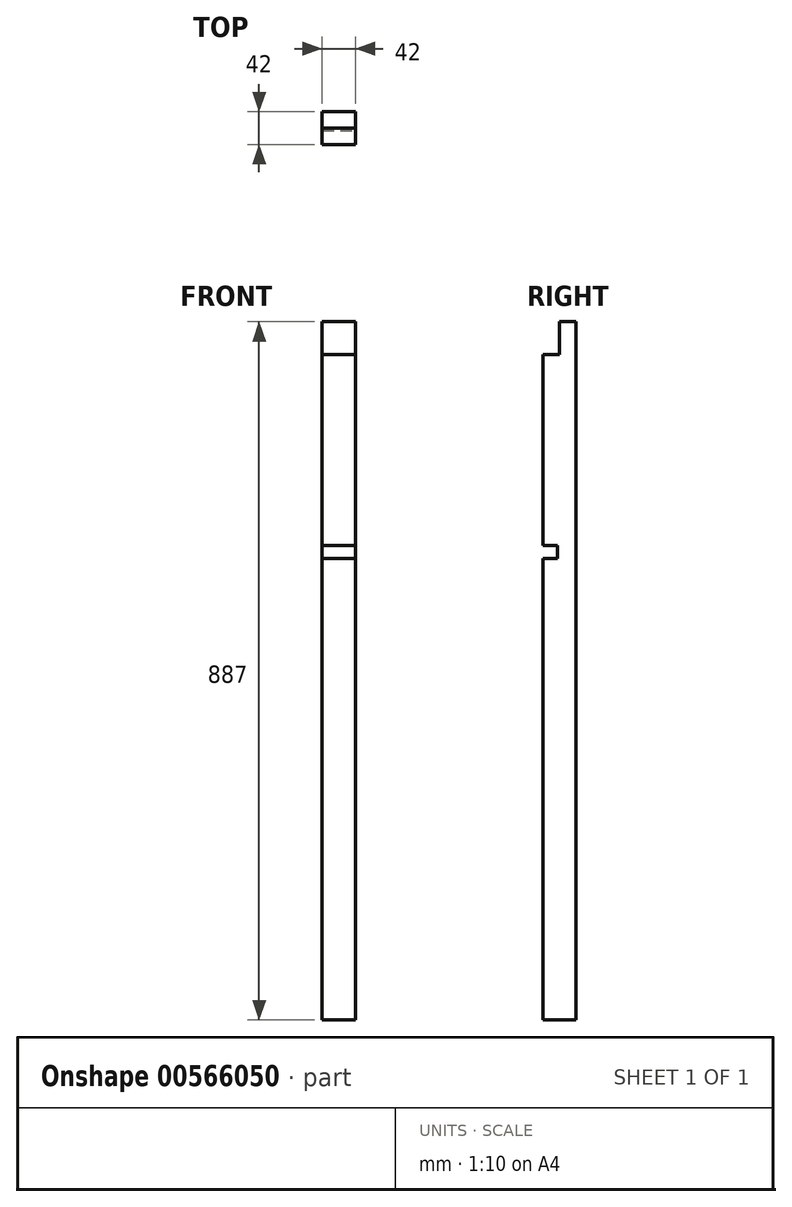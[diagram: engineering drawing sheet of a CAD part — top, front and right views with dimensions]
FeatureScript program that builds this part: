
annotation { "Feature Type Name" : "Feature", "Feature Type Description" : "" }
export const myFeature = defineFeature(function(context is Context, id is Id, definition is map)
    precondition{}
    {
        {
            var Q0;
            Q0=qCreatedBy(makeId("Top.planeOp"),FACE);
            var sketch = newSketch(context, id + "F0", { "sketchPlane" : qUnion([Q0])});
            skLineSegment(sketch, "E0.bottom", {"start": v(-55.79, 37.72) * mm, "end": v(-13.79, 37.72) * mm});
            skLineSegment(sketch, "E0.top", {"start": v(-55.79, -4.28) * mm, "end": v(-13.79, -4.28) * mm});
            skLineSegment(sketch, "E0.left", {"start": v(-55.79, 37.72) * mm, "end": v(-55.79, -4.28) * mm});
            skLineSegment(sketch, "E0.right", {"start": v(-13.79, 37.72) * mm, "end": v(-13.79, -4.28) * mm});
            skSolve(sketch);
        }
        {
            var Q0;
            Q0=qSketchRegion(id+"F0",true);
            extrude(context, id + "F1", {"entities" : qUnion([Q0]), "depth" : 887 * mm, "offsetDistance" : 25 * mm});
        }
        {
            var Q0;
            Q0=makeQuery(id+"F1.opExtrude","SWEPT_FACE",FACE,{"disambiguationData":[OSD([sQuery(id+"F0.wireOp",EDGE,"E0.right")])]});
            var sketch = newSketch(context, id + "F2", { "sketchPlane" : qUnion([Q0])});
            skLineSegment(sketch, "E1.bottom", {"start": v(16.72, 887) * mm, "end": v(-4.28, 887) * mm});
            skLineSegment(sketch, "E1.top", {"start": v(16.72, 845.4) * mm, "end": v(-4.28, 845.4) * mm});
            skLineSegment(sketch, "E1.left", {"start": v(16.72, 887) * mm, "end": v(16.72, 845.4) * mm});
            skLineSegment(sketch, "E1.right", {"start": v(-4.28, 887) * mm, "end": v(-4.28, 845.4) * mm});
            skSolve(sketch);
        }
        {
            var Q0;
            Q0=qSketchRegion(id+"F2",true);
            extrude(context, id + "F3", {"entities" : qUnion([Q0]), "operationType" : NewBodyOperationType.REMOVE, "oppositeDirection" : true, "depth" : 42 * mm, "offsetDistance" : 25 * mm});
        }
        {
            var Q0;
            Q0=makeQuery(id+"F1.opExtrude","SWEPT_FACE",FACE,{"disambiguationData":[OSD([sQuery(id+"F0.wireOp",EDGE,"E0.right")])]});
            var sketch = newSketch(context, id + "F4", { "sketchPlane" : qUnion([Q0])});
            skLineSegment(sketch, "E2.bottom", {"start": v(-4.28, 585.99) * mm, "end": v(13.72, 585.99) * mm});
            skLineSegment(sketch, "E2.top", {"start": v(-4.28, 602.99) * mm, "end": v(13.72, 602.99) * mm});
            skLineSegment(sketch, "E2.left", {"start": v(-4.28, 585.99) * mm, "end": v(-4.28, 602.99) * mm});
            skLineSegment(sketch, "E2.right", {"start": v(13.72, 585.99) * mm, "end": v(13.72, 602.99) * mm});
            skSolve(sketch);
        }
        {
            var Q0;
            Q0=makeQuery(id+"F4.imprint","IMPRINT",FACE,{"disambiguationData":[TD([[makeQuery(id+"F4.imprint","IMPRINT",EDGE,{"derivedFrom":sQuery(id+"F4.wireOp",EDGE,"E2.bottom")}),1.0]])]});
            extrude(context, id + "F5", {"entities" : qUnion([Q0]), "operationType" : NewBodyOperationType.REMOVE, "oppositeDirection" : true, "depth" : 42 * mm, "offsetDistance" : 25 * mm});
        }
    });
